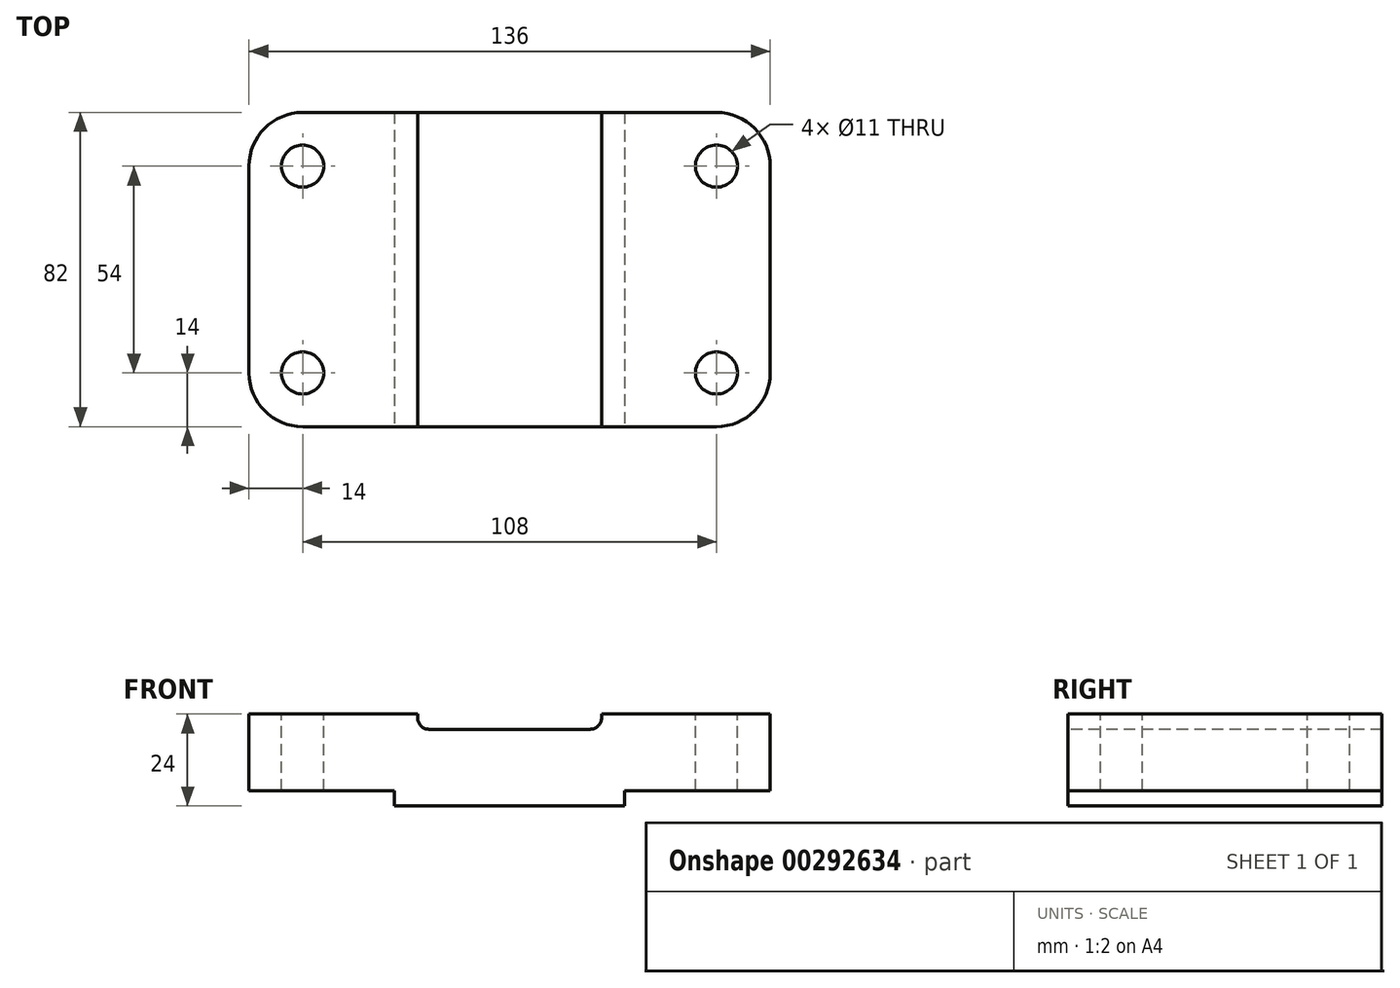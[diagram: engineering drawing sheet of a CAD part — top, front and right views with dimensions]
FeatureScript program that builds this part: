
annotation { "Feature Type Name" : "Feature", "Feature Type Description" : "" }
export const myFeature = defineFeature(function(context is Context, id is Id, definition is map)
    precondition{}
    {
        {
            var Q0;
            Q0=qCreatedBy(makeId("Top.planeOp"),FACE);
            var sketch = newSketch(context, id + "F0", { "sketchPlane" : qUnion([Q0])});
            skLineSegment(sketch, "E0.bottom", {"start": v(0, 0) * mm, "end": v(136, 0) * mm});
            skLineSegment(sketch, "E0.top", {"start": v(0, 82) * mm, "end": v(136, 82) * mm});
            skLineSegment(sketch, "E0.left", {"start": v(0, 0) * mm, "end": v(0, 82) * mm});
            skLineSegment(sketch, "E0.right", {"start": v(136, 0) * mm, "end": v(136, 82) * mm});
            skSolve(sketch);
        }
        {
            var Q0;
            Q0 = qSketchRegion(id + "F0", true);
            extrude(context, id + "F1", {"entities" : qUnion([Q0]), "depth" : 24 * mm});
        }
        {
            var Q0;
            Q0=makeQuery(id+"F1.opExtrude","SWEPT_EDGE",EDGE,{"disambiguationData":[OSD([sQuery(id+"F0.wireOp",EDGE,"E0.bottom"),sQuery(id+"F0.wireOp",EDGE,"E0.left")])]});
            var Q1;
            Q1=makeQuery(id+"F1.opExtrude","SWEPT_EDGE",EDGE,{"disambiguationData":[OSD([sQuery(id+"F0.wireOp",EDGE,"E0.bottom"),sQuery(id+"F0.wireOp",EDGE,"E0.right")])]});
            var Q2;
            Q2=makeQuery(id+"F1.opExtrude","SWEPT_EDGE",EDGE,{"disambiguationData":[OSD([sQuery(id+"F0.wireOp",EDGE,"E0.top"),sQuery(id+"F0.wireOp",EDGE,"E0.right")])]});
            var Q3;
            Q3=makeQuery(id+"F1.opExtrude","SWEPT_EDGE",EDGE,{"disambiguationData":[OSD([sQuery(id+"F0.wireOp",EDGE,"E0.top"),sQuery(id+"F0.wireOp",EDGE,"E0.left")])]});
            fillet(context, id + "F2", {"entities" : qUnion([Q0, Q1, Q2, Q3]), "radius" : 14 * mm, "tangentPropagation" : true, "allowEdgeOverflow" : false});
        }
        {
            var Q0;
            Q0=qCreatedBy(makeId("Front.planeOp"),FACE);
            var sketch = newSketch(context, id + "F3", { "sketchPlane" : qUnion([Q0])});
            skLineSegment(sketch, "E1", {"start": v(44, 24) * mm, "end": v(92, 24) * mm});
            skLineSegment(sketch, "E2", {"start": v(44, 24) * mm, "end": v(44, 20) * mm});
            skLineSegment(sketch, "E3", {"start": v(44, 20) * mm, "end": v(92, 20) * mm});
            skLineSegment(sketch, "E4", {"start": v(92, 20) * mm, "end": v(92, 24) * mm});
            skSolve(sketch);
        }
        {
            var Q0;
            Q0 = qSketchRegion(id + "F3", true);
            extrude(context, id + "F4", {"entities" : qUnion([Q0]), "operationType" : NewBodyOperationType.REMOVE, "endBound" : BoundingType.THROUGH_ALL, "oppositeDirection" : true, "depth" : 25 * mm});
        }
        {
            var Q0;
            Q0=makeQuery(id+"F4.boolean.opBoolean","COPY",EDGE,{"derivedFrom":makeQuery(id+"F4.opExtrude","SWEPT_EDGE",EDGE,{"disambiguationData":[OSD([sQuery(id+"F3.wireOp",EDGE,"E2"),sQuery(id+"F3.wireOp",EDGE,"E3")])]})});
            var Q1;
            Q1=makeQuery(id+"F4.boolean.opBoolean","COPY",EDGE,{"derivedFrom":makeQuery(id+"F4.opExtrude","SWEPT_EDGE",EDGE,{"disambiguationData":[OSD([sQuery(id+"F3.wireOp",EDGE,"E3"),sQuery(id+"F3.wireOp",EDGE,"E4")])]})});
            fillet(context, id + "F5", {"entities" : qUnion([Q0, Q1]), "radius" : 3 * mm, "tangentPropagation" : true, "allowEdgeOverflow" : false});
        }
        {
            var Q0;
            Q0=qCreatedBy(makeId("Front.planeOp"),FACE);
            var sketch = newSketch(context, id + "F6", { "sketchPlane" : qUnion([Q0])});
            skLineSegment(sketch, "E5", {"start": v(0, 0) * mm, "end": v(0, 4) * mm});
            skLineSegment(sketch, "E6", {"start": v(0, 4) * mm, "end": v(38, 4) * mm});
            skLineSegment(sketch, "E7", {"start": v(38, 4) * mm, "end": v(38, 0) * mm});
            skLineSegment(sketch, "E8", {"start": v(38, 0) * mm, "end": v(0, 0) * mm});
            skLineSegment(sketch, "E9.bottom", {"start": v(136, 0) * mm, "end": v(98, 0) * mm});
            skLineSegment(sketch, "E9.top", {"start": v(136, 4) * mm, "end": v(98, 4) * mm});
            skLineSegment(sketch, "E9.left", {"start": v(136, 0) * mm, "end": v(136, 4) * mm});
            skLineSegment(sketch, "E9.right", {"start": v(98, 0) * mm, "end": v(98, 4) * mm});
            skSolve(sketch);
        }
        {
            var Q0;
            Q0 = qSketchRegion(id + "F6", true);
            extrude(context, id + "F7", {"entities" : qUnion([Q0]), "operationType" : NewBodyOperationType.REMOVE, "endBound" : BoundingType.THROUGH_ALL, "oppositeDirection" : true, "depth" : 25 * mm});
        }
        {
            var Q0;
            {var subQ0=sQuery(id+"F0.wireOp",EDGE,"E0.left");var subQ1=sQuery(id+"F0.wireOp",EDGE,"E0.bottom");var subQ2=sQuery(id+"F0.wireOp",EDGE,"E0.top");Q0=makeQuery(id+"F4.boolean.opBoolean","SPLIT",FACE,{"disambiguationData":[TD([makeQuery(id+"F1.opExtrude","SWEPT_FACE",FACE,{"disambiguationData":[OSD([subQ0])]})])],"derivedFrom":makeQuery(id+"F1.opExtrude","CAP_FACE",FACE,{"disambiguationData":[OSD([subQ1,subQ2,subQ0,sQuery(id+"F0.wireOp",EDGE,"E0.right")])],"isStart":false})});}
            var sketch = newSketch(context, id + "F8", { "sketchPlane" : qUnion([Q0])});
            skCircle(sketch, "E10", {"center": v(14, 68) * mm, "radius": 5.5 * mm});
            skCircle(sketch, "E11", {"center": v(14, 14) * mm, "radius": 5.5 * mm});
            skLineSegment(sketch, "E12", {"start": v(0, 14) * mm, "end": v(141.98, 14) * mm, "construction": true});
            skLineSegment(sketch, "E13", {"start": v(141.98, 68) * mm, "end": v(0, 68) * mm, "construction": true});
            skLineSegment(sketch, "E14", {"start": v(14, 82) * mm, "end": v(14, 0) * mm, "construction": true});
            skLineSegment(sketch, "E15", {"start": v(14, 0) * mm, "end": v(122, 0) * mm, "construction": true});
            skLineSegment(sketch, "E16", {"start": v(122, 0) * mm, "end": v(122, 82) * mm, "construction": true});
            skCircle(sketch, "E17", {"center": v(122, 68) * mm, "radius": 5.5 * mm});
            skCircle(sketch, "E18", {"center": v(122, 14) * mm, "radius": 5.5 * mm});
            skSolve(sketch);
        }
        {
            var Q0;
            Q0 = qSketchRegion(id + "F8", true);
            extrude(context, id + "F9", {"entities" : qUnion([Q0]), "operationType" : NewBodyOperationType.REMOVE, "endBound" : BoundingType.THROUGH_ALL, "oppositeDirection" : true, "depth" : 25 * mm});
        }
    });
